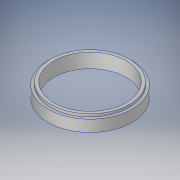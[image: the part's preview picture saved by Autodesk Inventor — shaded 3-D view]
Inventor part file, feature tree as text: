
AUTODESK INVENTOR PART (.ipt)
format: ipt  version: 2017 SP1 (Build 210196100, 196)  size: 153,088 bytes
history: native  units: in
note: dims shown in document units (in); Inventor stores cm internally (conversion verified against a paired STEP export)
features: revolve x1, sketch x1
ambient origin geometry x8: Origin, YZ Plane, XZ Plane, XY Plane, X Axis, Y Axis, Z Axis, Center Point
bodies: Body1 (feature_tree)
feature tree (2):
  revolve  "Revolution3"  [1 undecoded]
  sketch  "Sketch1"  dims[d0=1.13in d3=0.1718in d5=1.0in d6=1.0in d7=90.0deg d8=0.5in d9=15.0deg d31=0.25in d34=15.0deg d37=1.75in d40=3.75in d41=0.125in d46=0.75in d47=0.5in d51=0.5in d52=0.25in d54=0.5in d55=0.5in d56=1.25in d58=0.0017in d59=0.5in d60=0.5in d61=1.0in d62=0.234in d63=0.234in d64=0.125in d67=0.25in d68=4.25in d69=0.25in d70=0.25in d71=0.125in d73=3.4in d74=1.25in d75=0.2498in d77=90.0deg]
note: 1 required parameter value undecoded (feature->parameter linkage not recoverable at this tier; creation-order binding heuristic only, values carry confidence <= 0.55)
